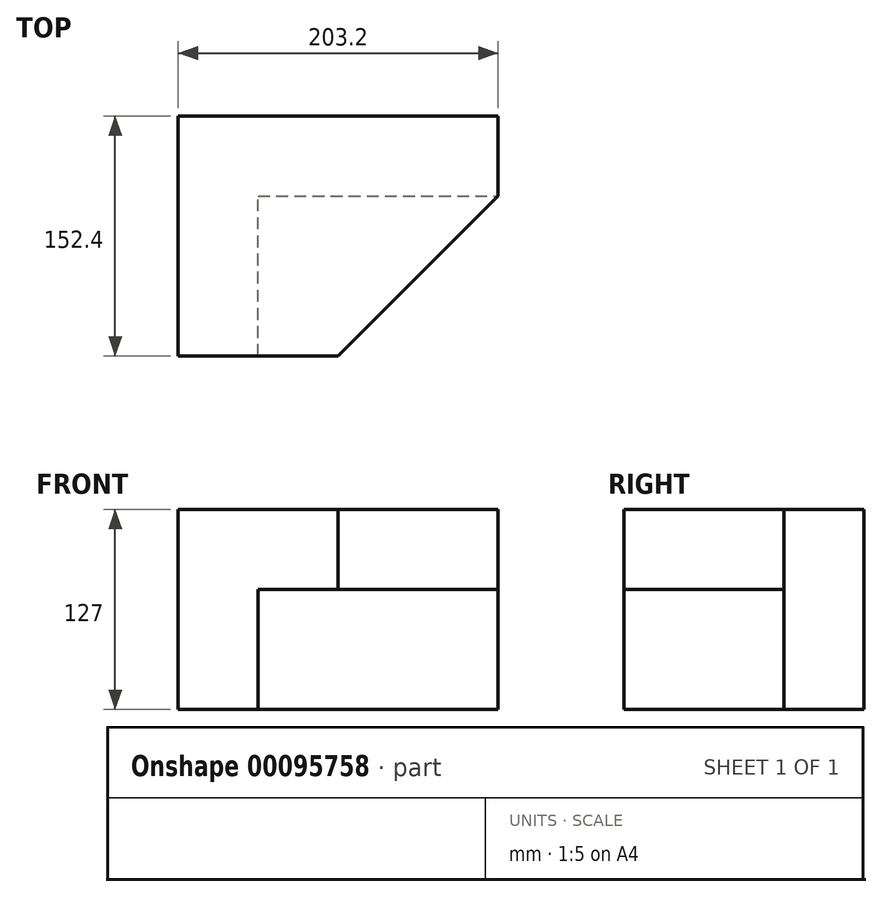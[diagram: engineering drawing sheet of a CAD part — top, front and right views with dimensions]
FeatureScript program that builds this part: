
annotation { "Feature Type Name" : "Feature", "Feature Type Description" : "" }
export const myFeature = defineFeature(function(context is Context, id is Id, definition is map)
    precondition{}
    {
        {
            var Q0;
            Q0=qCreatedBy(makeId("Front.planeOp"),FACE);
            var sketch = newSketch(context, id + "F0", { "sketchPlane" : qUnion([Q0])});
            skLineSegment(sketch, "E0.bottom", {"start": v(-133.04, 71.67) * mm, "end": v(70.16, 71.67) * mm});
            skLineSegment(sketch, "E0.top", {"start": v(-133.04, -55.33) * mm, "end": v(70.16, -55.33) * mm});
            skLineSegment(sketch, "E0.left", {"start": v(-133.04, 71.67) * mm, "end": v(-133.04, -55.33) * mm});
            skLineSegment(sketch, "E0.right", {"start": v(70.16, 71.67) * mm, "end": v(70.16, -55.33) * mm});
            skSolve(sketch);
        }
        {
            var Q0;
            Q0 = qSketchRegion(id + "F0", true);
            extrude(context, id + "F1", {"entities" : qUnion([Q0]), "depth" : 50.8 * mm});
        }
        {
            var Q0;
            Q0=makeQuery(id+"F1.opExtrude","CAP_FACE",FACE,{"disambiguationData":[OSD([sQuery(id+"F0.wireOp",EDGE,"E0.bottom"),sQuery(id+"F0.wireOp",EDGE,"E0.top"),sQuery(id+"F0.wireOp",EDGE,"E0.left"),sQuery(id+"F0.wireOp",EDGE,"E0.right")])],"isStart":false});
            var sketch = newSketch(context, id + "F2", { "sketchPlane" : qUnion([Q0])});
            skLineSegment(sketch, "E1.bottom", {"start": v(-133.04, -55.33) * mm, "end": v(-82.24, -55.33) * mm});
            skLineSegment(sketch, "E1.top", {"start": v(-133.04, 71.67) * mm, "end": v(-82.24, 71.67) * mm});
            skLineSegment(sketch, "E1.left", {"start": v(-133.04, -55.33) * mm, "end": v(-133.04, 71.67) * mm});
            skLineSegment(sketch, "E1.right", {"start": v(-82.24, -55.33) * mm, "end": v(-82.24, 71.67) * mm});
            skLineSegment(sketch, "E2.bottom", {"start": v(-133.04, 71.67) * mm, "end": v(-31.44, 71.67) * mm});
            skLineSegment(sketch, "E2.top", {"start": v(-133.04, 20.87) * mm, "end": v(-31.44, 20.87) * mm});
            skLineSegment(sketch, "E2.left", {"start": v(-133.04, 71.67) * mm, "end": v(-133.04, 20.87) * mm});
            skLineSegment(sketch, "E2.right", {"start": v(-31.44, 71.67) * mm, "end": v(-31.44, 20.87) * mm});
            skSolve(sketch);
        }
        {
            var Q0;
            Q0 = qSketchRegion(id + "F2", true);
            extrude(context, id + "F3", {"entities" : qUnion([Q0]), "operationType" : NewBodyOperationType.ADD, "depth" : 101.6 * mm});
        }
        {
            var Q0;
            Q0=makeQuery(id+"F3.boolean.opBoolean","MERGE",FACE,{"derivedFrom":[makeQuery(id+"F1.opExtrude","SWEPT_FACE",FACE,{"disambiguationData":[OSD([sQuery(id+"F0.wireOp",EDGE,"E0.bottom")])]}),makeQuery(id+"F3.opExtrude","SWEPT_FACE",FACE,{"disambiguationData":[OSD([sQuery(id+"F2.wireOp",EDGE,"E2.bottom")])]})]});
            var sketch = newSketch(context, id + "F4", { "sketchPlane" : qUnion([Q0])});
            skLineSegment(sketch, "E3", {"start": v(-31.44, -152.4) * mm, "end": v(70.16, -50.8) * mm});
            skLineSegment(sketch, "E4", {"start": v(70.16, -50.8) * mm, "end": v(-31.44, -50.8) * mm});
            skLineSegment(sketch, "E5", {"start": v(-31.44, -50.8) * mm, "end": v(-31.44, -152.4) * mm});
            skSolve(sketch);
        }
        {
            var Q0;
            Q0=makeQuery(id+"F4.imprint","IMPRINT",FACE,{"disambiguationData":[TD([[makeQuery(id+"F4.imprint","IMPRINT",EDGE,{"derivedFrom":sQuery(id+"F4.wireOp",EDGE,"E3")}),1.0]])]});
            extrude(context, id + "F5", {"entities" : qUnion([Q0]), "operationType" : NewBodyOperationType.ADD, "oppositeDirection" : true, "depth" : 50.8 * mm});
        }
    });
